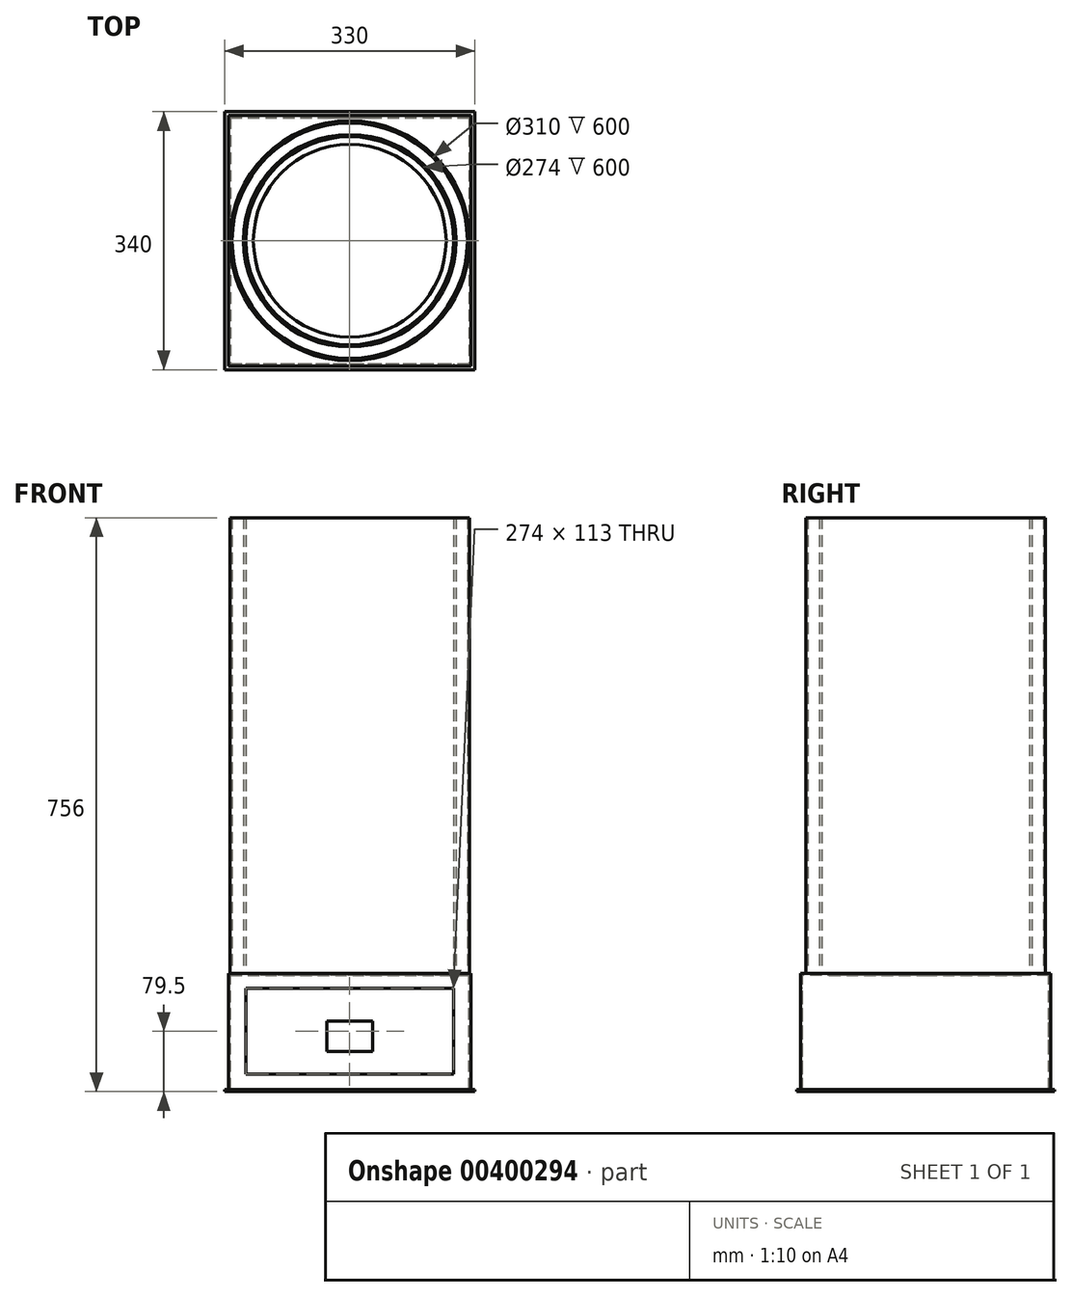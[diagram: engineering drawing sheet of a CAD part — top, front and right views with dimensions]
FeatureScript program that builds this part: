
annotation { "Feature Type Name" : "Feature", "Feature Type Description" : "" }
export const myFeature = defineFeature(function(context is Context, id is Id, definition is map)
    precondition{}
    {
        {
            var Q0;
            Q0=qCreatedBy(makeId("Top.planeOp"),FACE);
            var sketch = newSketch(context, id + "F0", { "sketchPlane" : qUnion([Q0])});
            skCircle(sketch, "E0", {"center": v(0, 0) * mm, "radius": 140 * mm});
            skCircle(sketch, "E1", {"center": v(0, 0) * mm, "radius": 137 * mm});
            skCircle(sketch, "E2", {"center": v(0, 0) * mm, "radius": 155 * mm});
            skCircle(sketch, "E3.0", {"center": v(0, 0) * mm, "radius": 158 * mm});
            skSolve(sketch);
        }
        {
            var Q0;
            Q0=makeQuery(id+"F0.imprint","IMPRINT",FACE,{"disambiguationData":[TD([[makeQuery(id+"F0.imprint","IMPRINT",EDGE,{"derivedFrom":sQuery(id+"F0.wireOp",EDGE,"E0")}),1.0]])]});
            extrude(context, id + "F1", {"entities" : qUnion([Q0]), "depth" : 600 * mm});
        }
        {
            var Q0;
            Q0=qCreatedBy(makeId("Top.planeOp"),FACE);
            var sketch = newSketch(context, id + "F2", { "sketchPlane" : qUnion([Q0])});
            skLineSegment(sketch, "E4.bottom", {"start": v(-160, 165) * mm, "end": v(160, 165) * mm});
            skLineSegment(sketch, "E4.top", {"start": v(-160, -165) * mm, "end": v(160, -165) * mm});
            skLineSegment(sketch, "E4.left", {"start": v(-160, 165) * mm, "end": v(-160, -165) * mm});
            skLineSegment(sketch, "E4.right", {"start": v(160, 165) * mm, "end": v(160, -165) * mm});
            skPoint(sketch, "E4.middle", {"position": v(0, 0) * mm});
            skLineSegment(sketch, "E5", {"start": v(0, 0) * mm, "end": v(0, 86.05) * mm, "construction": true});
            skCircle(sketch, "E6", {"center": v(0, 0) * mm, "radius": 127 * mm});
            skSolve(sketch);
        }
        {
            var Q0;
            Q0=makeQuery(id+"F2.imprint","IMPRINT",FACE,{"disambiguationData":[TD([[makeQuery(id+"F2.imprint","IMPRINT",EDGE,{"derivedFrom":sQuery(id+"F2.wireOp",EDGE,"E4.bottom")}),-1.0]])]});
            extrude(context, id + "F3", {"entities" : qUnion([Q0]), "oppositeDirection" : true, "depth" : 3 * mm});
        }
        {
            var Q0;
            Q0=makeQuery(id+"F0.imprint","IMPRINT",FACE,{"disambiguationData":[TD([[makeQuery(id+"F0.imprint","IMPRINT",EDGE,{"derivedFrom":sQuery(id+"F0.wireOp",EDGE,"E2")}),-1.0]])]});
            extrude(context, id + "F4", {"entities" : qUnion([Q0]), "depth" : 600 * mm});
        }
        {
            var Q0;
            Q0=makeQuery(id+"F3.opExtrude","CAP_FACE",FACE,{"disambiguationData":[OSD([sQuery(id+"F2.wireOp",EDGE,"E4.bottom"),sQuery(id+"F2.wireOp",EDGE,"E4.top"),sQuery(id+"F2.wireOp",EDGE,"E4.left"),sQuery(id+"F2.wireOp",EDGE,"E4.right"),sQuery(id+"F2.wireOp",EDGE,"E6")])],"isStart":false});
            var sketch = newSketch(context, id + "F5", { "sketchPlane" : qUnion([Q0])});
            skLineSegment(sketch, "E7.0", {"start": v(-157, 162) * mm, "end": v(157, 162) * mm});
            skLineSegment(sketch, "E7.1", {"start": v(-157, -162) * mm, "end": v(-157, 162) * mm});
            skLineSegment(sketch, "E7.2", {"start": v(-157, -162) * mm, "end": v(157, -162) * mm});
            skLineSegment(sketch, "E7.3", {"start": v(157, -162) * mm, "end": v(157, 162) * mm});
            skSolve(sketch);
        }
        {
            var Q0;
            Q0=makeQuery(id+"F5.imprint","IMPRINT",FACE,{"disambiguationData":[TD([[makeQuery(id+"F5.imprint","IMPRINT",EDGE,{"derivedFrom":sQuery(id+"F5.wireOp",EDGE,"E7.0")}),1.0]])]});
            extrude(context, id + "F6", {"entities" : qUnion([Q0]), "operationType" : NewBodyOperationType.ADD, "depth" : 150 * mm});
        }
        {
            var Q0;
            Q0=makeQuery(id+"F6.opExtrude","CAP_FACE",FACE,{"disambiguationData":[OSD([sQuery(id+"F2.wireOp",EDGE,"E4.bottom"),sQuery(id+"F2.wireOp",EDGE,"E4.top"),sQuery(id+"F2.wireOp",EDGE,"E4.left"),sQuery(id+"F2.wireOp",EDGE,"E4.right"),sQuery(id+"F5.wireOp",EDGE,"E7.0"),sQuery(id+"F5.wireOp",EDGE,"E7.1"),sQuery(id+"F5.wireOp",EDGE,"E7.2"),sQuery(id+"F5.wireOp",EDGE,"E7.3")])],"isStart":false});
            var sketch = newSketch(context, id + "F7", { "sketchPlane" : qUnion([Q0])});
            skLineSegment(sketch, "E8.0", {"start": v(-165, -170) * mm, "end": v(-165, 170) * mm});
            skLineSegment(sketch, "E8.1", {"start": v(-165, -170) * mm, "end": v(165, -170) * mm});
            skLineSegment(sketch, "E8.2", {"start": v(165, -170) * mm, "end": v(165, 170) * mm});
            skLineSegment(sketch, "E8.3", {"start": v(-165, 170) * mm, "end": v(165, 170) * mm});
            skSolve(sketch);
        }
        {
            var Q0;
            Q0 = qSketchRegion(id + "F7", true);
            extrude(context, id + "F8", {"entities" : qUnion([Q0]), "depth" : 3 * mm});
        }
        {
            var Q0;
            {var subQ0=sQuery(id+"F2.wireOp",EDGE,"E4.top");Q0=makeQuery(id+"F6.boolean.opBoolean","MERGE",FACE,{"derivedFrom":[makeQuery(id+"F3.opExtrude","SWEPT_FACE",FACE,{"disambiguationData":[OSD([subQ0])]}),makeQuery(id+"F6.opExtrude","SWEPT_FACE",FACE,{"disambiguationData":[OSD([subQ0])]})]});}
            var sketch = newSketch(context, id + "F9", { "sketchPlane" : qUnion([Q0])});
            skLineSegment(sketch, "E9.bottom", {"start": v(-137, -133) * mm, "end": v(137, -133) * mm});
            skLineSegment(sketch, "E9.top", {"start": v(-137, -20) * mm, "end": v(137, -20) * mm});
            skLineSegment(sketch, "E9.left", {"start": v(-137, -133) * mm, "end": v(-137, -20) * mm});
            skLineSegment(sketch, "E9.right", {"start": v(137, -133) * mm, "end": v(137, -20) * mm});
            skSolve(sketch);
        }
        {
            var Q0;
            Q0=makeQuery(id+"F9.imprint","IMPRINT",FACE,{"disambiguationData":[TD([[makeQuery(id+"F9.imprint","IMPRINT",EDGE,{"derivedFrom":sQuery(id+"F9.wireOp",EDGE,"E9.bottom")}),1.0]])]});
            extrude(context, id + "F10", {"entities" : qUnion([Q0]), "operationType" : NewBodyOperationType.REMOVE, "oppositeDirection" : true, "depth" : 25 * mm});
        }
        {
            var Q0;
            Q0=makeQuery(id+"F6.opExtrude","SWEPT_FACE",FACE,{"disambiguationData":[OSD([sQuery(id+"F2.wireOp",EDGE,"E4.bottom")])]});
            var sketch = newSketch(context, id + "F11", { "sketchPlane" : qUnion([Q0])});
            skLineSegment(sketch, "E10.bottom", {"start": v(-30, -63) * mm, "end": v(30, -63) * mm});
            skLineSegment(sketch, "E10.top", {"start": v(-30, -103) * mm, "end": v(30, -103) * mm});
            skLineSegment(sketch, "E10.left", {"start": v(-30, -63) * mm, "end": v(-30, -103) * mm});
            skLineSegment(sketch, "E10.right", {"start": v(30, -63) * mm, "end": v(30, -103) * mm});
            skLineSegment(sketch, "E11", {"start": v(0, 0) * mm, "end": v(0, -164.01) * mm, "construction": true});
            skSolve(sketch);
        }
        {
            var Q0;
            Q0=makeQuery(id+"F11.imprint","IMPRINT",FACE,{"disambiguationData":[TD([[makeQuery(id+"F11.imprint","IMPRINT",EDGE,{"derivedFrom":sQuery(id+"F11.wireOp",EDGE,"E10.bottom")}),-1.0]])]});
            extrude(context, id + "F12", {"entities" : qUnion([Q0]), "operationType" : NewBodyOperationType.REMOVE, "oppositeDirection" : true, "depth" : 4 * mm});
        }
    });
